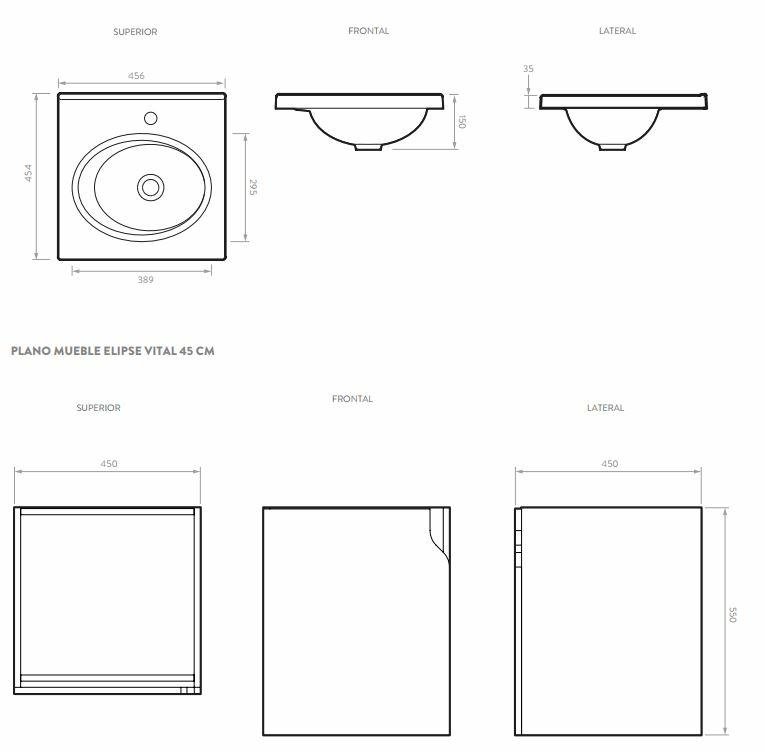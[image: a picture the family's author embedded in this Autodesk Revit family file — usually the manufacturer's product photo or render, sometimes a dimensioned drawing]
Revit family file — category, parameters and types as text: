
# Revit family: LM0026611_Mueble Elipse Vital 45 cm con Lavamanos
name_source: partatom
category: Plumbing Fixtures
units: mm (PartAtom-declared; Revit-internal decimal feet)

## family parameters
Always vertical = Yes
Cut with Voids When Loaded = No
OmniClass Number = 23.45.05.14.14
OmniClass Title = Sinks/Lavatories
Part Type = Normal
Room Calculation Point = No
Round Connector Dimension = Use Diameter
Shared = No
Work Plane-Based = No

## types (2) — shared parameters
Alto = 850 mm  [stored 2.78871 ft]
Ancho = 445 mm  [stored 1.45997 ft]
Description = La línea de muebles Elipse Vital compacto que se se adapta a la gran
mayoría de espacios disponibles
diseño y funcionalidad, ALUVIA se inspira en el movimiento y caída del agua en la
naturaleza, es por ello de sus formas orgánicas donde podemos obtener un producto
compacto y de líneas fluidas, que se adapta en espacios pequeños.
el pricipal benefico de los muebles de esta linea es ser un producto compacto que cuenta
con cajón y repisa brindándole al consumidor mayor capacidad de almacenamiento, como
una excelente solución para aquellos espacios pequeños.
Dimensiones Generales (H * W * P) = 21,65” x 17,72” x 17,72” (550,0 x 450 x 450 mm)
Garantia Madera = 5 año
Manufacturer = Corona
Material Lavamanos = Corona_Cerámica_Sinterizada
Peso Bruto aprox = 24,0 lb (10,9 kg)
Peso Neto aprox = 22,5 lb (10,2 kg)
Profundidad = 435 mm  [stored 1.42717 ft]
Resistencia a la humedad = 8%
Resistencia al rayado = 700 ciclos

## per-type parameters (varying)
| type | Canto | Carga máxima | Densidad | Garantia Herrajes | Material | Model | URL |
| Ref. 604281711 Mueble Aluvia Miel Con Lavamanos |  |  |  |  | Corona_Madera_Carbon |  | https://corona.co |
| Ref. 604286091 Mueble Aluvia Habano Con Lavamanos | PVC rígido 2 mm de calibre. | 99,2 lb (45 kg). | 15 mms 670 kg./m^3. | 1 año | <By Category> | Mueble aluvia miel LVM 45X45 |  |

note: [stored X ft] marks values corroborated as IEEE doubles in the binary element streams (Revit-internal decimal feet)

## geometry (parser evidence)
native form markers: Sweep x26
no freeform markers — native parametric forms only
